# Revit family: Legrand Coffret XL³ 400 Isolant
name_source: partatom
category: Equipement électrique
units: mm (PartAtom-declared; Revit-internal decimal feet)

## family parameters
Basée sur le plan de construction = Non
Configuration du panneau = Deux colonnes, circuits au sein
Cote de connecteur circulaire = Utiliser le diamètre
Couper avec des vides une fois chargée = Non
Numéro OmniClass = 23.80.30.11.17
Partagée = Non
Point de calcul de pièce = Non
Titre OmniClass = Distribution Boards and Control Panels
Toujours verticalement = Oui
Type d'élément = Tableau de raccordement

## types (5) — shared parameters
Conditions Générale d'Utilisation = https://export.legrand.com
Fabricant = Legrand
Finition = Peinture époxipolyester déposée par poudrage électrostatique
ICW (jusqu'à) (kA) = 25
IK avec porte = 08
IK sans porte = 07
IN (A) = 400
IP avec porte = 40
IP sans porte = 30
IPK (kA) = 52.5
Largeur (mm) = 575 mm
Largeur zone d'installation = 1245 mm
Matière = Acier
Matière coin = Plastique
Modèle = XL³ 400 Isolant
RAL = 7035
URL = https://www.legrand.fr
poignée Coffret = Oui
poignée Tableau = Non
profondeur (mm) = 175 mm  [stored 0.574147 ft]
profondeur zone d'installation = 750 mm  [stored 2.46063 ft]
zero-valued in all types: Elévation par défaut

## per-type parameters (varying)
| type | Hauteur (mm) | Hauteur zone d'installation |
| 020153-020253 | 600 mm | 600 mm |
| 020154-020254 | 750 mm  [stored 2.46063 ft] | 750 mm  [stored 2.46063 ft] |
| 020155-020255 | 900 mm  [stored 2.95276 ft] | 900 mm  [stored 2.95276 ft] |
| 020156-020256 | 1050 mm | 1050 mm |
| 020157-020257 | 1200 mm | 1200 mm |

note: [stored X ft] marks values corroborated as IEEE doubles in the binary element streams (Revit-internal decimal feet)
